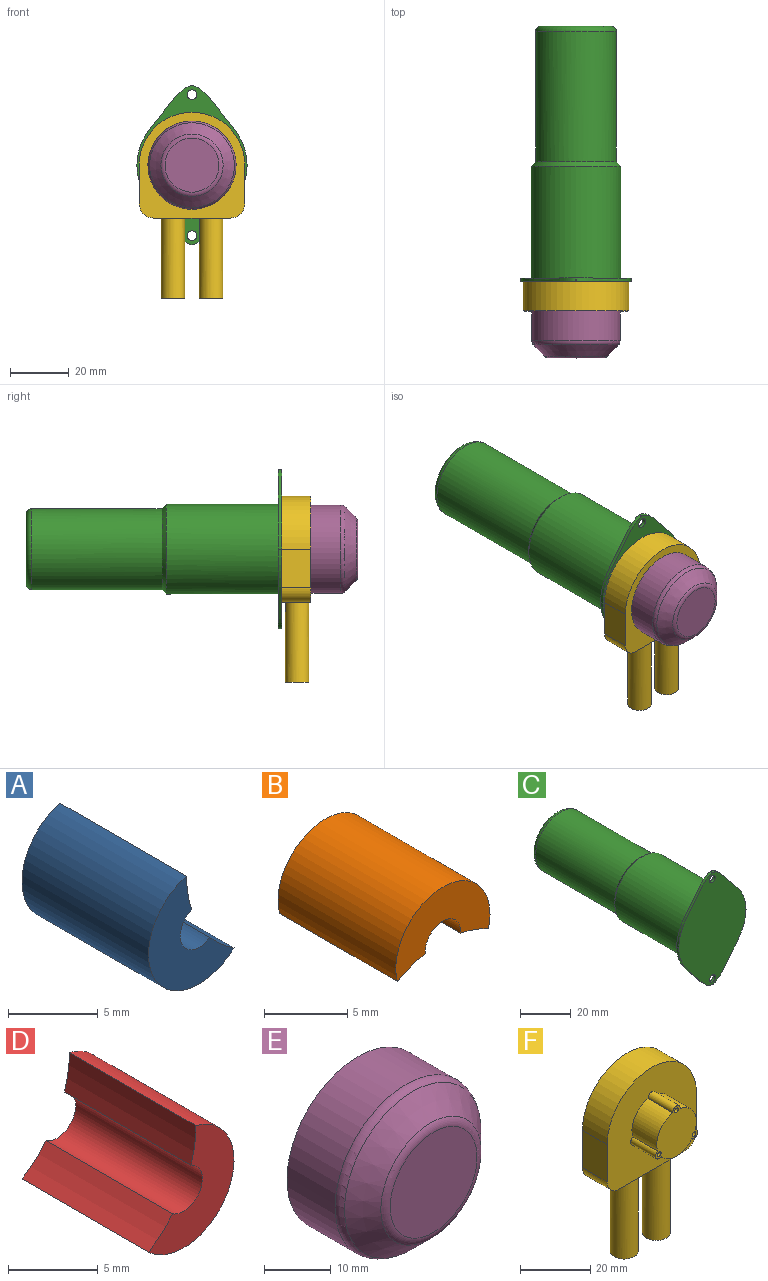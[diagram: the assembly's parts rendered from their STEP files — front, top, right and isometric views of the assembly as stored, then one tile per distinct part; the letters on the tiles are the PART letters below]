
ASSEMBLY  parts=6 mates=5
PART A: 6 faces, bbox 6.8x10x7.9 mm
  f0: cylinder r=8mm len=10mm, axis (0,1,0), area 25.4mm2, adj f1,f3,f4,f5
  f1: cylinder r=4mm len=10mm, axis (0,1,0), area 145.9mm2, adj f0,f2,f4,f5
  f2: cylinder r=8mm len=10mm, axis (0,1,0), area 25.4mm2, adj f1,f3,f4,f5
  f3: cylinder r=1.5mm len=10mm, axis (0,1,0), area 49.9mm2, adj f0,f2,f4,f5
  f4: plane 7.87x6.75mm, normal (0,-1,0), area 24.1mm2, adj f0,f1,f2,f3
  f5: plane 7.87x6.75mm, normal (0,1,0), area 24.1mm2, adj f0,f1,f2,f3
PART B: 6 faces, bbox 8x10x5 mm
  f0: cylinder r=8mm len=10mm, axis (0,1,0), area 25.4mm2, adj f1,f3,f4,f5
  f1: cylinder r=4mm len=10mm, axis (0,1,0), area 145.9mm2, adj f0,f2,f4,f5
  f2: cylinder r=8mm len=10mm, axis (0,1,0), area 25.4mm2, adj f1,f3,f4,f5
  f3: cylinder r=1.5mm len=10mm, axis (0,1,0), area 49.9mm2, adj f0,f2,f4,f5
  f4: plane 8x5mm, normal (0,-1,0), area 24.1mm2, adj f0,f1,f2,f3
  f5: plane 8x5mm, normal (0,1,0), area 24.1mm2, adj f0,f1,f2,f3
PART C: 14 faces, bbox 37.5x86.9x54 mm
  f0: cylinder r=2mm len=1.16mm, axis (0,1,0), area 0.3mm2, adj f1,f5,f7,f8
  f1: extruded ~27x18.62mm, area 39.6mm2, adj f0,f2,f7,f8
  f2: extruded ~27x18.75mm, area 39.7mm2, adj f1,f3,f7,f8
  f3: extruded ~27x18.75mm, area 39.7mm2, adj f2,f5,f7,f8
  f4: cylinder r=1.65mm len=3.3mm, axis (0,1,0), area 12mm2, adj f7,f8
  f5: extruded ~27x18.62mm, area 39.6mm2, adj f0,f3,f7,f8
  f6: cylinder r=1.65mm len=3.3mm, axis (0,1,0), area 12mm2, adj f7,f8
  f7: plane 54x37.5mm, normal (0,-1,0), area 1334.1mm2, adj f0,f1,f2,f3,f4,f5,f6
  f8: plane 54x37.5mm, normal (0,1,0), area 603.5mm2, adj f0,f1,f2,f3,f4,f5,f6,f9
  f9: cylinder r=15.25mm len=38mm, axis (0,-1,0), area 3641.1mm2, adj f8,f12
  f10: cylinder r=13.75mm len=44.25mm, axis (0,-1,0), area 3822.9mm2, adj f12,f13
  f11: plane 23.5x23.5mm, normal (0,1,0), area 433.7mm2, adj f13
  f12: cone r=13.25mm half-angle=45deg, axis (0,-1,0), area 193.3mm2, adj f9,f10
  f13: torus R=11.75mm, axis (0,1,0), area 257.1mm2, adj f10,f11
PART D: 6 faces, bbox 6.8x10x7.9 mm
  f0: cylinder r=8mm len=10mm, axis (0,1,0), area 25.4mm2, adj f1,f3,f4,f5
  f1: cylinder r=4mm len=10mm, axis (0,1,0), area 145.9mm2, adj f0,f2,f4,f5
  f2: cylinder r=8mm len=10mm, axis (0,1,0), area 25.4mm2, adj f1,f3,f4,f5
  f3: cylinder r=1.5mm len=10mm, axis (0,1,0), area 49.9mm2, adj f0,f2,f4,f5
  f4: plane 7.87x6.75mm, normal (0,-1,0), area 24.1mm2, adj f0,f1,f2,f3
  f5: plane 7.87x6.75mm, normal (0,1,0), area 24.1mm2, adj f0,f1,f2,f3
PART E: 6 faces, bbox 32.5x16x32.5 mm
  f0: cylinder r=15mm len=30mm, axis (0,1,0), area 958.6mm2, adj f2,f4
  f1: plane 18.34x18.34mm, normal (0,-1,0), area 264.3mm2, adj f5
  f2: plane 30x30mm, normal (0,1,0), area 706.9mm2, adj f0
  f3: cone r=10mm half-angle=45deg, axis (0,1,0), area 425.2mm2, adj f4,f5
  f4: torus R=13mm, axis (0,-1,0), area 146.1mm2, adj f0,f3
  f5: torus R=9.17mm, axis (0,-1,0), area 97.9mm2, adj f1,f3
PART F: 29 faces, bbox 36x20x63.3 mm
  f0: plane 36x36mm, normal (0,-1,0), area 934.1mm2, adj f1,f2,f3,f4,f5,f6,f8,f9
  f1: cylinder r=18mm len=36mm, axis (0,1,0), area 565.5mm2, adj f0,f2,f6,f7
  f2: plane 13x10mm, normal (-1,0,0), area 130mm2, adj f0,f1,f3,f7
  f3: cylinder r=5mm len=10mm, axis (0,1,0), area 78.5mm2, adj f0,f2,f4,f7
  f4: plane 26x10mm, normal (0,0,-1), area 159.5mm2, adj f0,f3,f5,f7,f22,f26
  f5: cylinder r=5mm len=10mm, axis (0,1,0), area 78.5mm2, adj f0,f4,f6,f7
  f6: plane 13x10mm, normal (1,0,0), area 130mm2, adj f0,f1,f5,f7
  f7: plane 36x36mm, normal (0,1,0), area 1146.2mm2, adj f1,f2,f3,f4,f5,f6
  f8: cylinder r=1.5mm len=10mm, axis (0,1,0), area 49.9mm2, adj f0,f9,f15,f17
  f9: cylinder r=8mm len=10.36mm, axis (0,1,0), area 136mm2, adj f0,f8,f10,f17
  f10: cylinder r=1.5mm len=10mm, axis (0,1,0), area 49.9mm2, adj f0,f9,f11,f17
  f11: cylinder r=8mm len=10.36mm, axis (0,1,0), area 136mm2, adj f0,f10,f12,f17
  f12: cylinder r=1.5mm len=10mm, axis (0,1,0), area 49.9mm2, adj f0,f11,f15,f17
  f13: cylinder r=0.75mm len=10mm, axis (0,1,0), area 47.1mm2, adj f17,f18
  f14: cylinder r=0.75mm len=10mm, axis (0,1,0), area 47.1mm2, adj f17,f19
  f15: cylinder r=8mm len=12.31mm, axis (0,1,0), area 140.4mm2, adj f0,f8,f12,f17
  f16: cylinder r=0.75mm len=10mm, axis (0,1,0), area 47.1mm2, adj f17,f20
  f17: plane 17.5x17mm, normal (0,-1,0), area 206.8mm2, adj f8,f9,f10,f11,f12,f13,f14,f15
  f18: plane 1.5x1.5mm, normal (0,-1,0), area 1.8mm2, adj f13
  f19: plane 1.5x1.5mm, normal (0,-1,0), area 1.8mm2, adj f14
  f20: plane 1.5x1.5mm, normal (0,-1,0), area 1.8mm2, adj f16
  f21: cylinder r=1.4mm len=27.25mm, axis (0,0,1), area 239.7mm2, adj f23,f24
  f22: cylinder r=4mm len=27.25mm, axis (0,0,1), area 684.9mm2, adj f4,f23
  f23: plane 8x8mm, normal (0,0,-1), area 44.1mm2, adj f21,f22
  f24: plane 2.8x2.8mm, normal (0,0,-1), area 6.2mm2, adj f21
  f25: cylinder r=1.4mm len=27.25mm, axis (0,0,1), area 239.7mm2, adj f27,f28
  f26: cylinder r=4mm len=27.25mm, axis (0,0,1), area 684.9mm2, adj f4,f27
  f27: plane 8x8mm, normal (0,0,-1), area 44.1mm2, adj f25,f26
  f28: plane 2.8x2.8mm, normal (0,0,-1), area 6.2mm2, adj f25
PLACE A t=(6.84,70.24,2.56)mm
PLACE B t=(6.84,70.24,2.56)mm
PLACE C t=(6.84,70.24,2.56)mm
PLACE D t=(6.84,70.24,2.56)mm
PLACE E t=(6.84,70.24,1.76)mm
PLACE F t=(6.84,70.24,2.56)mm
MATE fastened B.f3 <-> F.f10  axis (0,1,0) through (6.84,59.08,10.56)mm
MATE fastened F.f1 <-> C.f10  axis (0,1,0) through (6.84,69.08,2.56)mm
MATE fastened D.f1 <-> F.f8  axis (0,1,0) through (13.84,59.08,-1.31)mm
MATE fastened A.f1 <-> F.f12  axis (0,1,0) through (-0.16,59.08,-1.31)mm
MATE fastened E.f0 <-> F.f11  axis (0,1,0) through (6.84,59.08,2.56)mm
